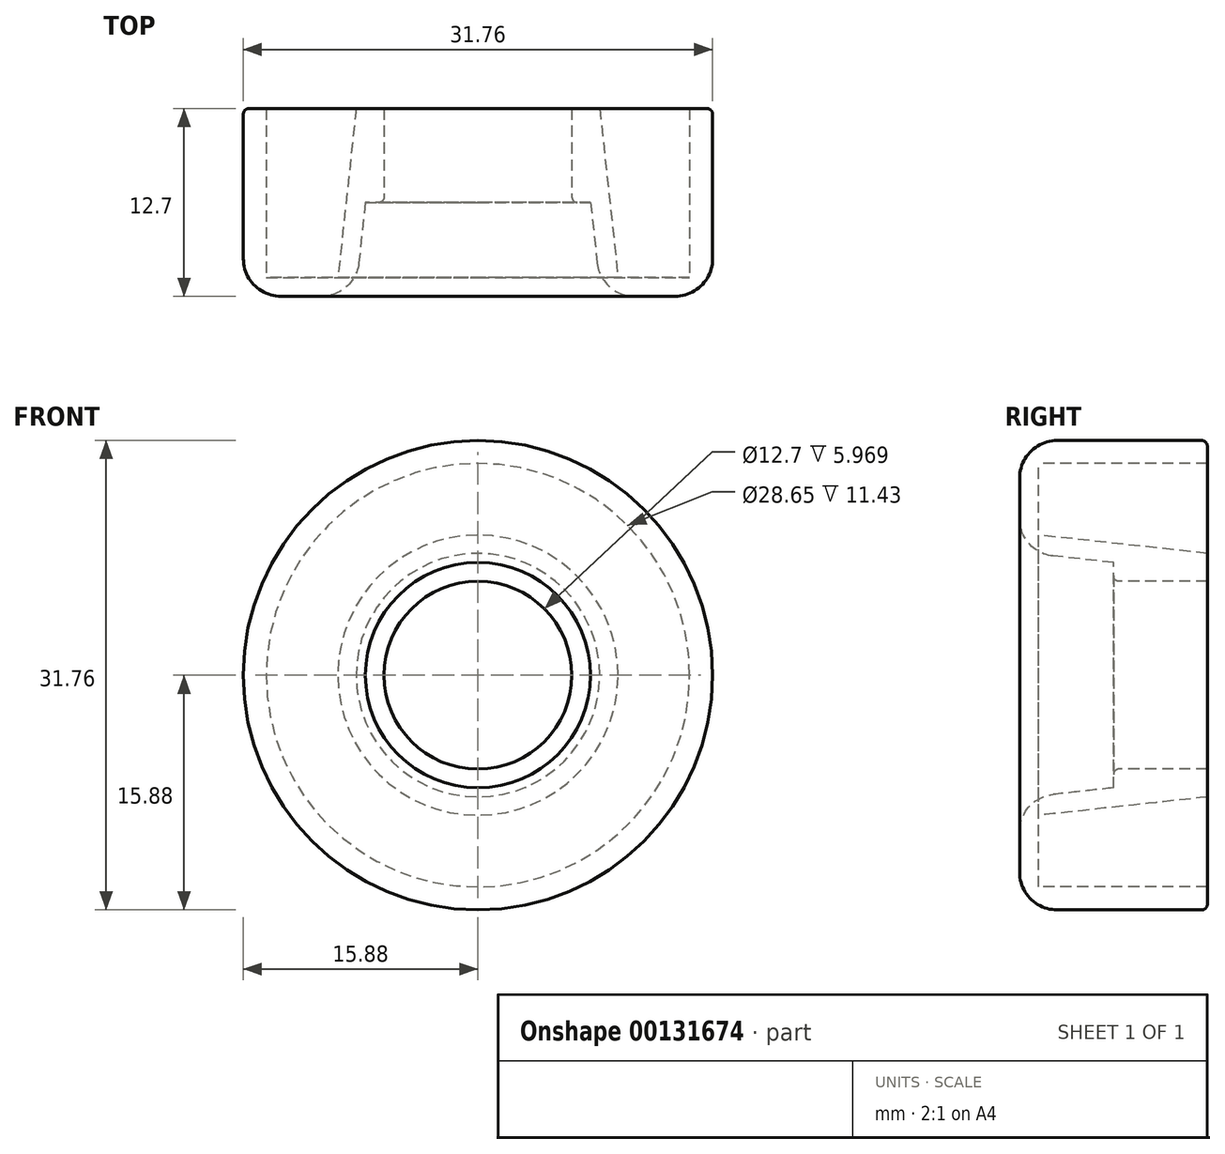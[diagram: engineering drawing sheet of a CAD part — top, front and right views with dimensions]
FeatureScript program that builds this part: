
annotation { "Feature Type Name" : "Feature", "Feature Type Description" : "" }
export const myFeature = defineFeature(function(context is Context, id is Id, definition is map)
    precondition{}
    {
        {
            var Q0;
            Q0=qCreatedBy(makeId("Front.planeOp"),FACE);
            var sketch = newSketch(context, id + "F0", { "sketchPlane" : qUnion([Q0])});
            skCircle(sketch, "E0", {"center": v(0, 0) * mm, "radius": 15.88 * mm});
            skSolve(sketch);
        }
        {
            var Q0;
            Q0=makeQuery(id+"F0.imprint","IMPRINT",FACE,{"disambiguationData":[TD([[makeQuery(id+"F0.imprint","IMPRINT",EDGE,{"derivedFrom":sQuery(id+"F0.wireOp",EDGE,"E0")}),1.0]])]});
            extrude(context, id + "F1", {"entities" : qUnion([Q0]), "depth" : 12.7 * mm});
        }
        {
            var Q0;
            Q0=qCreatedBy(makeId("Top.planeOp"),FACE);
            var sketch = newSketch(context, id + "F2", { "sketchPlane" : qUnion([Q0])});
            skLineSegment(sketch, "E1", {"start": v(0, 0) * mm, "end": v(0, -12.7) * mm});
            skLineSegment(sketch, "E2", {"start": v(0, -12.7) * mm, "end": v(-8.31, -12.7) * mm});
            skLineSegment(sketch, "E3", {"start": v(-8.31, -12.7) * mm, "end": v(-7.62, -6.35) * mm});
            skLineSegment(sketch, "E4", {"start": v(-7.62, -6.35) * mm, "end": v(-6.35, -6.35) * mm});
            skLineSegment(sketch, "E5", {"start": v(-6.35, -6.35) * mm, "end": v(-6.35, 0) * mm});
            skLineSegment(sketch, "E6", {"start": v(-6.35, 0) * mm, "end": v(0, 0) * mm});
            skLineSegment(sketch, "E7", {"start": v(-8.24, 0) * mm, "end": v(-9.48, -11.43) * mm});
            skLineSegment(sketch, "E8", {"start": v(-9.48, -11.43) * mm, "end": v(-14.32, -11.43) * mm});
            skLineSegment(sketch, "E9", {"start": v(-14.32, -11.43) * mm, "end": v(-14.32, 0) * mm});
            skLineSegment(sketch, "E10", {"start": v(-14.32, 0) * mm, "end": v(-8.24, 0) * mm});
            skSolve(sketch);
        }
        {
            var Q0;
            Q0 = qSketchRegion(id + "F2", true);
            var Q1;
            Q1=sQuery(id+"F2.wireOp",EDGE,"E1");
            revolve(context, id + "F3", {"operationType" : NewBodyOperationType.REMOVE, "entities" : qUnion([Q0]), "axis" : qUnion([Q1]), "revolveType" : RevolveType.FULL, "oppositeDirection" : true});
        }
        {
            var Q0;
            Q0=makeQuery(id+"F1.opExtrude","CAP_FACE",FACE,{"disambiguationData":[OSD([sQuery(id+"F0.wireOp",EDGE,"E0")])],"isStart":false});
            fillet(context, id + "F4", {"entities" : qUnion([Q0]), "radius" : 2.54 * mm, "tangentPropagation" : true, "allowEdgeOverflow" : false});
        }
        {
            var Q0;
            Q0=makeQuery(id+"F1.opExtrude","CAP_EDGE",EDGE,{"disambiguationData":[OSD([sQuery(id+"F0.wireOp",EDGE,"E0")])],"isStart":true});
            var Q1;
            Q1=makeQuery(id+"F3.boolean.opBoolean","COPY",EDGE,{"derivedFrom":makeQuery(id+"F3.opRevolve","SWEPT_EDGE",EDGE,{"disambiguationData":[OSD([sQuery(id+"F2.wireOp",EDGE,"E4"),sQuery(id+"F2.wireOp",EDGE,"E5")])]})});
            fillet(context, id + "F5", {"entities" : qUnion([Q0, Q1]), "radius" : 0.38 * mm, "tangentPropagation" : true, "allowEdgeOverflow" : false});
        }
    });
